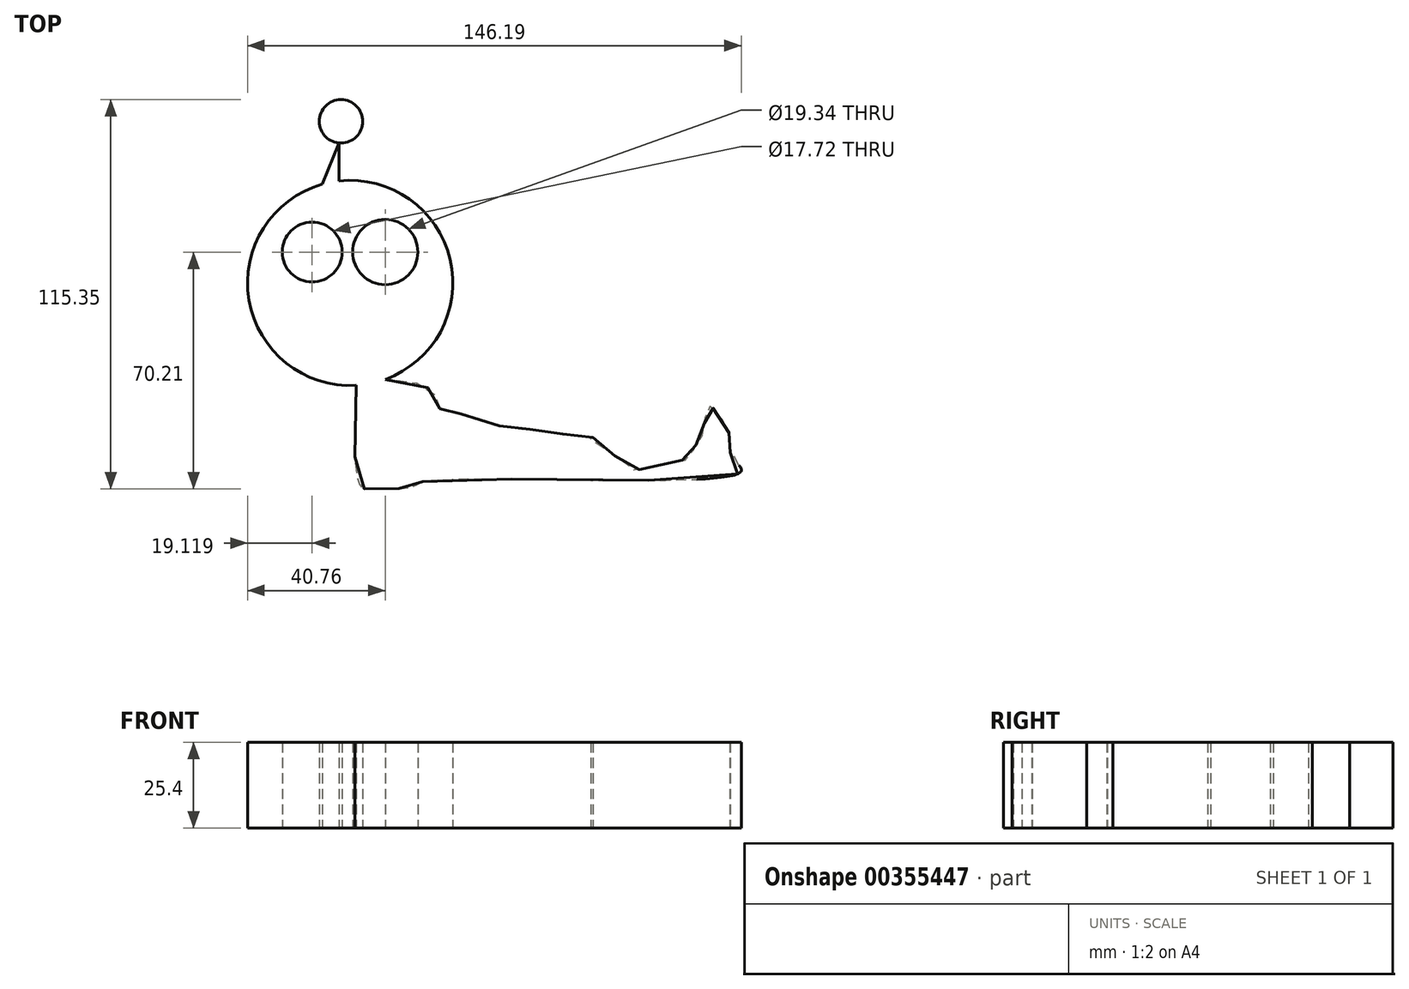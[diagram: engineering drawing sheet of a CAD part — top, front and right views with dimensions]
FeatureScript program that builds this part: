
annotation { "Feature Type Name" : "Feature", "Feature Type Description" : "" }
export const myFeature = defineFeature(function(context is Context, id is Id, definition is map)
    precondition{}
    {
        {
            var Q0;
            Q0=qCreatedBy(makeId("Top.planeOp"),FACE);
            var sketch = newSketch(context, id + "F0", { "sketchPlane" : qUnion([Q0])});
            skCircle(sketch, "E0", {"center": v(-10.36, 32.16) * mm, "radius": 30.4 * mm});
            skLineSegment(sketch, "E1", {"start": v(-18.69, 61.4) * mm, "end": v(-13.72, 73.6) * mm});
            skLineSegment(sketch, "E2", {"start": v(-13.72, 73.6) * mm, "end": v(-13.72, 62.37) * mm});
            skCircle(sketch, "E3", {"center": v(-13.1, 80.01) * mm, "radius": 6.43 * mm});
            skCircle(sketch, "E4", {"center": v(-21.64, 41.3) * mm, "radius": 8.86 * mm});
            skPoint(sketch, "E5.center.orphan", {"position": v(4.57, 41.3) * mm});
            skCircle(sketch, "E6", {"center": v(0, 41.3) * mm, "radius": 9.67 * mm});
            skLineSegment(sketch, "E7", {"start": v(-16.26, 19.92) * mm, "end": v(-4.55, 19.92) * mm});
            skFitSpline(sketch, "E8", {"points": [v(-8.6, 1.81) * mm, v(-7.48, -27.9) * mm, v(-3.58, -28.87) * mm, v(8.13, -28.22) * mm, v(11.71, -26.6) * mm, v(105.07, -24) * mm, v(102.79, -19.44) * mm, v(102.14, -14.56) * mm, v(101.81, -12.28) * mm, v(97.9, -5.78) * mm, v(95.3, -4.48) * mm, v(94.33, -11.3) * mm, v(92.7, -14.56) * mm, v(89.13, -20.41) * mm, v(87.83, -20.41) * mm, v(73.84, -23.34) * mm, v(73.19, -22.7) * mm, v(60.83, -13.9) * mm, v(61.48, -13.58) * mm, v(54.65, -12.93) * mm, v(43.91, -11.3) * mm, v(37.4, -10.98) * mm, v(23.75, -7.08) * mm, v(17.9, -5.45) * mm, v(15.94, -4.8) * mm, v(13.99, 0) * mm, v(0, 3.58) * mm], "startDerivative": vector(-19.32, -530.74) * mm, "endDerivative": vector(-340, 27.58) * mm});
            skSolve(sketch);
        }
        {
            var Q0;
            Q0 = qSketchRegion(id + "F0", true);
            extrude(context, id + "F1", {"entities" : qUnion([Q0]), "depth" : 25.4 * mm});
        }
    });
